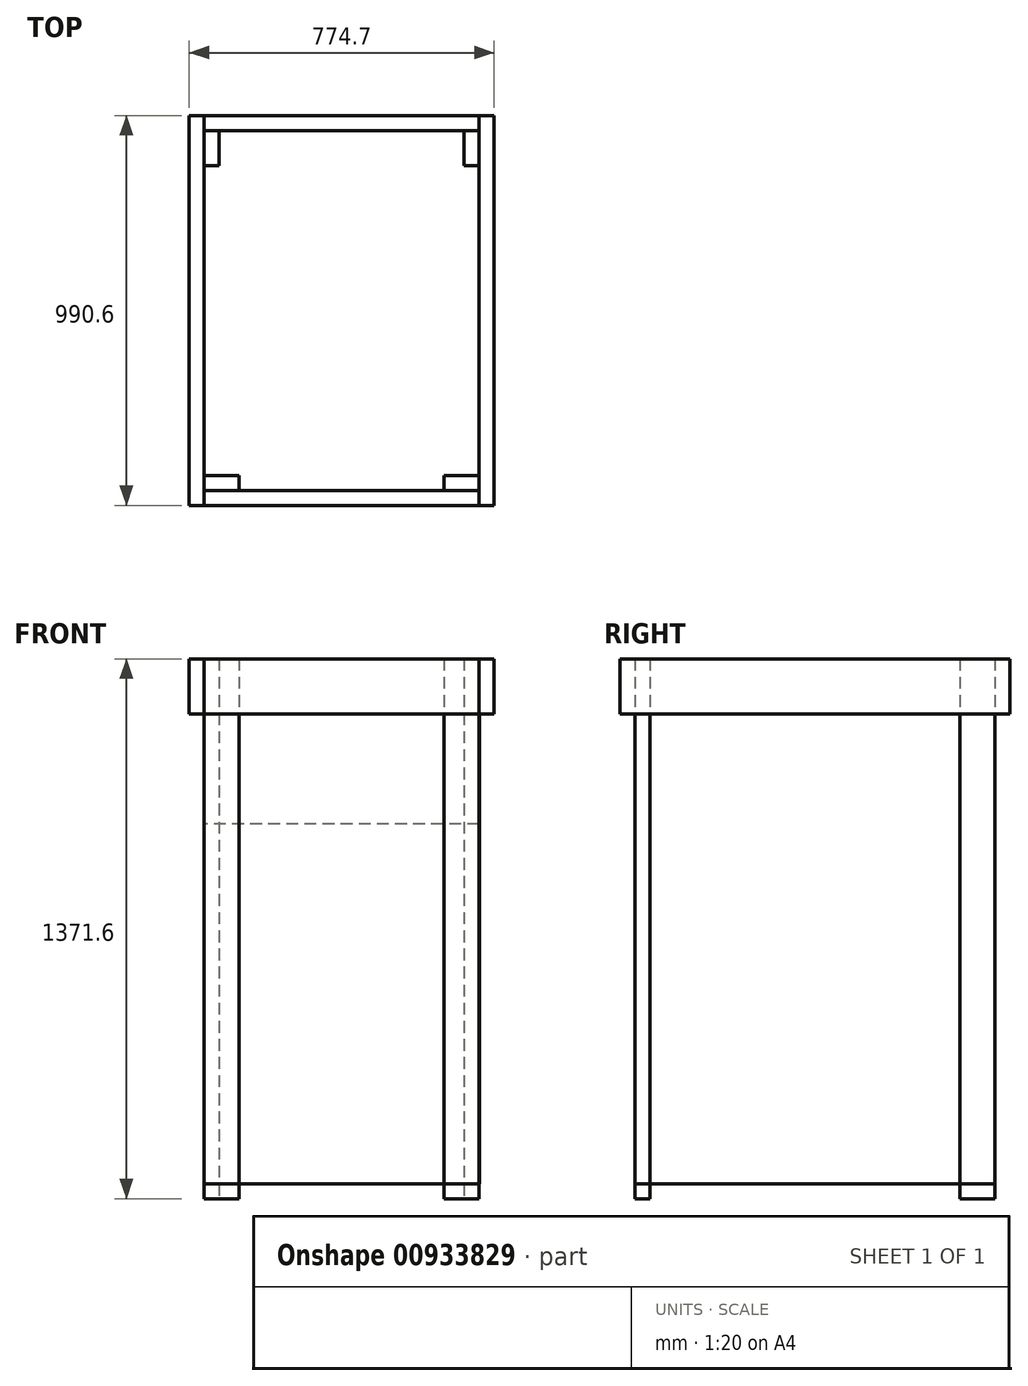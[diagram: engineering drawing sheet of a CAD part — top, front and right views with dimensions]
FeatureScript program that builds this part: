
annotation { "Feature Type Name" : "Feature", "Feature Type Description" : "" }
export const myFeature = defineFeature(function(context is Context, id is Id, definition is map)
    precondition{}
    {
        {
            var Q0;
            Q0=qCreatedBy(makeId("Top.planeOp"),FACE);
            var sketch = newSketch(context, id + "F0", { "sketchPlane" : qUnion([Q0])});
            skLineSegment(sketch, "E0.rect.bottom", {"start": v(349.25, 457.2) * mm, "end": v(-349.25, 457.2) * mm, "construction": true});
            skLineSegment(sketch, "E0.rect.top", {"start": v(349.25, -457.2) * mm, "end": v(-349.25, -457.2) * mm, "construction": true});
            skLineSegment(sketch, "E0.rect.left", {"start": v(349.25, 457.2) * mm, "end": v(349.25, -457.2) * mm, "construction": true});
            skLineSegment(sketch, "E0.rect.right", {"start": v(-349.25, 457.2) * mm, "end": v(-349.25, -457.2) * mm, "construction": true});
            skPoint(sketch, "E0.rect.middle", {"position": v(0, 0) * mm});
            skLineSegment(sketch, "E1.bottom", {"start": v(-349.25, 457.2) * mm, "end": v(-311.15, 457.2) * mm});
            skLineSegment(sketch, "E1.top", {"start": v(-349.25, 368.3) * mm, "end": v(-311.15, 368.3) * mm});
            skLineSegment(sketch, "E1.left", {"start": v(-349.25, 457.2) * mm, "end": v(-349.25, 368.3) * mm});
            skLineSegment(sketch, "E1.right", {"start": v(-311.15, 457.2) * mm, "end": v(-311.15, 368.3) * mm});
            skLineSegment(sketch, "E2", {"start": v(0, 457.2) * mm, "end": v(0, -457.2) * mm, "construction": true});
            skLineSegment(sketch, "E3.bottom", {"start": v(-349.25, -457.2) * mm, "end": v(-260.35, -457.2) * mm});
            skLineSegment(sketch, "E3.top", {"start": v(-349.25, -419.1) * mm, "end": v(-260.35, -419.1) * mm});
            skLineSegment(sketch, "E3.left", {"start": v(-349.25, -457.2) * mm, "end": v(-349.25, -419.1) * mm});
            skLineSegment(sketch, "E3.right", {"start": v(-260.35, -457.2) * mm, "end": v(-260.35, -419.1) * mm});
            skLineSegment(sketch, "E4.0.MirrorCS", {"start": v(311.15, 457.2) * mm, "end": v(311.15, 368.3) * mm});
            skLineSegment(sketch, "E5.0.MirrorCS", {"start": v(349.25, 457.2) * mm, "end": v(311.15, 457.2) * mm});
            skLineSegment(sketch, "E6.0.MirrorCS", {"start": v(349.25, 457.2) * mm, "end": v(349.25, 368.3) * mm});
            skLineSegment(sketch, "E7.0.MirrorCS", {"start": v(349.25, 368.3) * mm, "end": v(311.15, 368.3) * mm});
            skLineSegment(sketch, "E8.0.MirrorCS", {"start": v(260.35, -457.2) * mm, "end": v(260.35, -419.1) * mm});
            skLineSegment(sketch, "E9.0.MirrorCS", {"start": v(349.25, -457.2) * mm, "end": v(260.35, -457.2) * mm});
            skLineSegment(sketch, "E10.0.MirrorCS", {"start": v(349.25, -419.1) * mm, "end": v(260.35, -419.1) * mm});
            skLineSegment(sketch, "E11.0.MirrorCS", {"start": v(349.25, -457.2) * mm, "end": v(349.25, -419.1) * mm});
            skSolve(sketch);
        }
        {
            var Q0;
            Q0=qSketchRegion(id+"F0",true);
            extrude(context, id + "F1", {"entities" : qUnion([Q0]), "depth" : 1371.6 * mm});
        }
        {
            var Q0;
            Q0=makeQuery(id+"F1.opExtrude","SWEPT_FACE",FACE,{"disambiguationData":[OSD([sQuery(id+"F0.wireOp",EDGE,"E1.left")])]});
            var sketch = newSketch(context, id + "F2", { "sketchPlane" : qUnion([Q0])});
            skLineSegment(sketch, "E12.bottom", {"start": v(-495.3, 1231.9) * mm, "end": v(495.3, 1231.9) * mm});
            skLineSegment(sketch, "E12.top", {"start": v(-495.3, 1371.6) * mm, "end": v(495.3, 1371.6) * mm});
            skLineSegment(sketch, "E12.left", {"start": v(-495.3, 1231.9) * mm, "end": v(-495.3, 1371.6) * mm});
            skLineSegment(sketch, "E12.right", {"start": v(495.3, 1231.9) * mm, "end": v(495.3, 1371.6) * mm});
            skSolve(sketch);
        }
        {
            var Q0;
            Q0=qSketchRegion(id+"F2",true);
            extrude(context, id + "F3", {"entities" : qUnion([Q0]), "depth" : 38.1 * mm});
        }
        {
            var Q0;
            Q0=makeQuery(id+"F1.opExtrude","SWEPT_FACE",FACE,{"disambiguationData":[OSD([sQuery(id+"F0.wireOp",EDGE,"E3.bottom")])]});
            var sketch = newSketch(context, id + "F4", { "sketchPlane" : qUnion([Q0])});
            skLineSegment(sketch, "E13.bottom", {"start": v(-349.25, 1231.9) * mm, "end": v(349.25, 1231.9) * mm});
            skLineSegment(sketch, "E13.top", {"start": v(-349.25, 1371.6) * mm, "end": v(349.25, 1371.6) * mm});
            skLineSegment(sketch, "E13.left", {"start": v(-349.25, 1231.9) * mm, "end": v(-349.25, 1371.6) * mm});
            skLineSegment(sketch, "E13.right", {"start": v(349.25, 1231.9) * mm, "end": v(349.25, 1371.6) * mm});
            skSolve(sketch);
        }
        {
            var Q0;
            Q0=qSketchRegion(id+"F4",true);
            extrude(context, id + "F5", {"entities" : qUnion([Q0]), "depth" : 38.1 * mm});
        }
        {
            var Q0;
            Q0=makeQuery(id+"F1.opExtrude","SWEPT_FACE",FACE,{"disambiguationData":[OSD([sQuery(id+"F0.wireOp",EDGE,"E1.left")])]});
            var sketch = newSketch(context, id + "F6", { "sketchPlane" : qUnion([Q0])});
            skLineSegment(sketch, "E14.bottom", {"start": v(-457.2, 1231.9) * mm, "end": v(457.2, 1231.9) * mm});
            skLineSegment(sketch, "E14.top", {"start": v(-457.2, 38.1) * mm, "end": v(457.2, 38.1) * mm});
            skLineSegment(sketch, "E14.left", {"start": v(-457.2, 1231.9) * mm, "end": v(-457.2, 38.1) * mm});
            skLineSegment(sketch, "E14.right", {"start": v(457.2, 1231.9) * mm, "end": v(457.2, 38.1) * mm});
            skSolve(sketch);
        }
        {
            var Q0;
            Q0=qSketchRegion(id+"F6",true);
            extrude(context, id + "F7", {"entities" : qUnion([Q0]), "depth" : 3 / 203.2 * mm});
        }
        {
            var Q0;
            Q0=makeQuery(id+"F1.opExtrude","SWEPT_FACE",FACE,{"disambiguationData":[OSD([sQuery(id+"F0.wireOp",EDGE,"E3.bottom")])]});
            var sketch = newSketch(context, id + "F8", { "sketchPlane" : qUnion([Q0])});
            skLineSegment(sketch, "E15.bottom", {"start": v(-349.25, 1231.9) * mm, "end": v(349.25, 1231.9) * mm});
            skLineSegment(sketch, "E15.top", {"start": v(-349.25, 38.1) * mm, "end": v(349.25, 38.1) * mm});
            skLineSegment(sketch, "E15.left", {"start": v(-349.25, 1231.9) * mm, "end": v(-349.25, 38.1) * mm});
            skLineSegment(sketch, "E15.right", {"start": v(349.25, 1231.9) * mm, "end": v(349.25, 38.1) * mm});
            skSolve(sketch);
        }
        {
            var Q0;
            Q0=qSketchRegion(id+"F8",true);
            extrude(context, id + "F9", {"entities" : qUnion([Q0]), "depth" : 3 / 203.2 * mm});
        }
        {
            var Q0;
            Q0=makeQuery(id+"F3.opExtrude","SWEPT_BODY",BODY,{"disambiguationData":[OSD([sQuery(id+"F2.wireOp",EDGE,"E12.bottom"),sQuery(id+"F2.wireOp",EDGE,"E12.top"),sQuery(id+"F2.wireOp",EDGE,"E12.left"),sQuery(id+"F2.wireOp",EDGE,"E12.right")])]});
            var Q1;
            Q1=makeQuery(id+"F7.opExtrude","SWEPT_BODY",BODY,{"disambiguationData":[OSD([sQuery(id+"F6.wireOp",EDGE,"E14.bottom"),sQuery(id+"F6.wireOp",EDGE,"E14.top"),sQuery(id+"F6.wireOp",EDGE,"E14.left"),sQuery(id+"F6.wireOp",EDGE,"E14.right")])]});
            var Q2;
            Q2=qCreatedBy(makeId("Right.planeOp"),FACE);
            mirror(context, id + "F10", {"entities" : qUnion([Q0, Q1]), "mirrorPlane" : qUnion([Q2])});
        }
        {
            var Q0;
            Q0=makeQuery(id+"F5.opExtrude","SWEPT_BODY",BODY,{"disambiguationData":[OSD([sQuery(id+"F4.wireOp",EDGE,"E13.bottom"),sQuery(id+"F4.wireOp",EDGE,"E13.top"),sQuery(id+"F4.wireOp",EDGE,"E13.left"),sQuery(id+"F4.wireOp",EDGE,"E13.right")])]});
            var Q1;
            Q1=makeQuery(id+"F9.opExtrude","SWEPT_BODY",BODY,{"disambiguationData":[OSD([sQuery(id+"F8.wireOp",EDGE,"E15.bottom"),sQuery(id+"F8.wireOp",EDGE,"E15.top"),sQuery(id+"F8.wireOp",EDGE,"E15.left"),sQuery(id+"F8.wireOp",EDGE,"E15.right")])]});
            var Q2;
            Q2=qCreatedBy(makeId("Front.planeOp"),FACE);
            mirror(context, id + "F11", {"entities" : qUnion([Q0, Q1]), "mirrorPlane" : qUnion([Q2])});
        }
        {
            var Q0;
            Q0=makeQuery(id+"F11.opPattern","COPY",FACE,{"derivedFrom":makeQuery(id+"F9.opExtrude","CAP_FACE",FACE,{"disambiguationData":[OSD([sQuery(id+"F8.wireOp",EDGE,"E15.bottom"),sQuery(id+"F8.wireOp",EDGE,"E15.top"),sQuery(id+"F8.wireOp",EDGE,"E15.left"),sQuery(id+"F8.wireOp",EDGE,"E15.right")])],"isStart":false}),"instanceName":"1"});
            var sketch = newSketch(context, id + "F12", { "sketchPlane" : qUnion([Q0])});
            skLineSegment(sketch, "E16.bottom", {"start": v(-349.25, 952.5) * mm, "end": v(349.25, 952.5) * mm});
            skLineSegment(sketch, "E16.top", {"start": v(-349.25, 38.1) * mm, "end": v(349.25, 38.1) * mm});
            skLineSegment(sketch, "E16.left", {"start": v(-349.25, 952.5) * mm, "end": v(-349.25, 38.1) * mm});
            skLineSegment(sketch, "E16.right", {"start": v(349.25, 952.5) * mm, "end": v(349.25, 38.1) * mm});
            skPoint(sketch, "E17", {"position": v(0, 38.1) * mm});
            skSolve(sketch);
        }
        {
            var Q0;
            Q0=qSketchRegion(id+"F12",true);
            extrude(context, id + "F13", {"entities" : qUnion([Q0]), "operationType" : NewBodyOperationType.REMOVE, "endBound" : BoundingType.UP_TO_NEXT, "oppositeDirection" : true, "depth" : 25.4 * mm});
        }
    });
